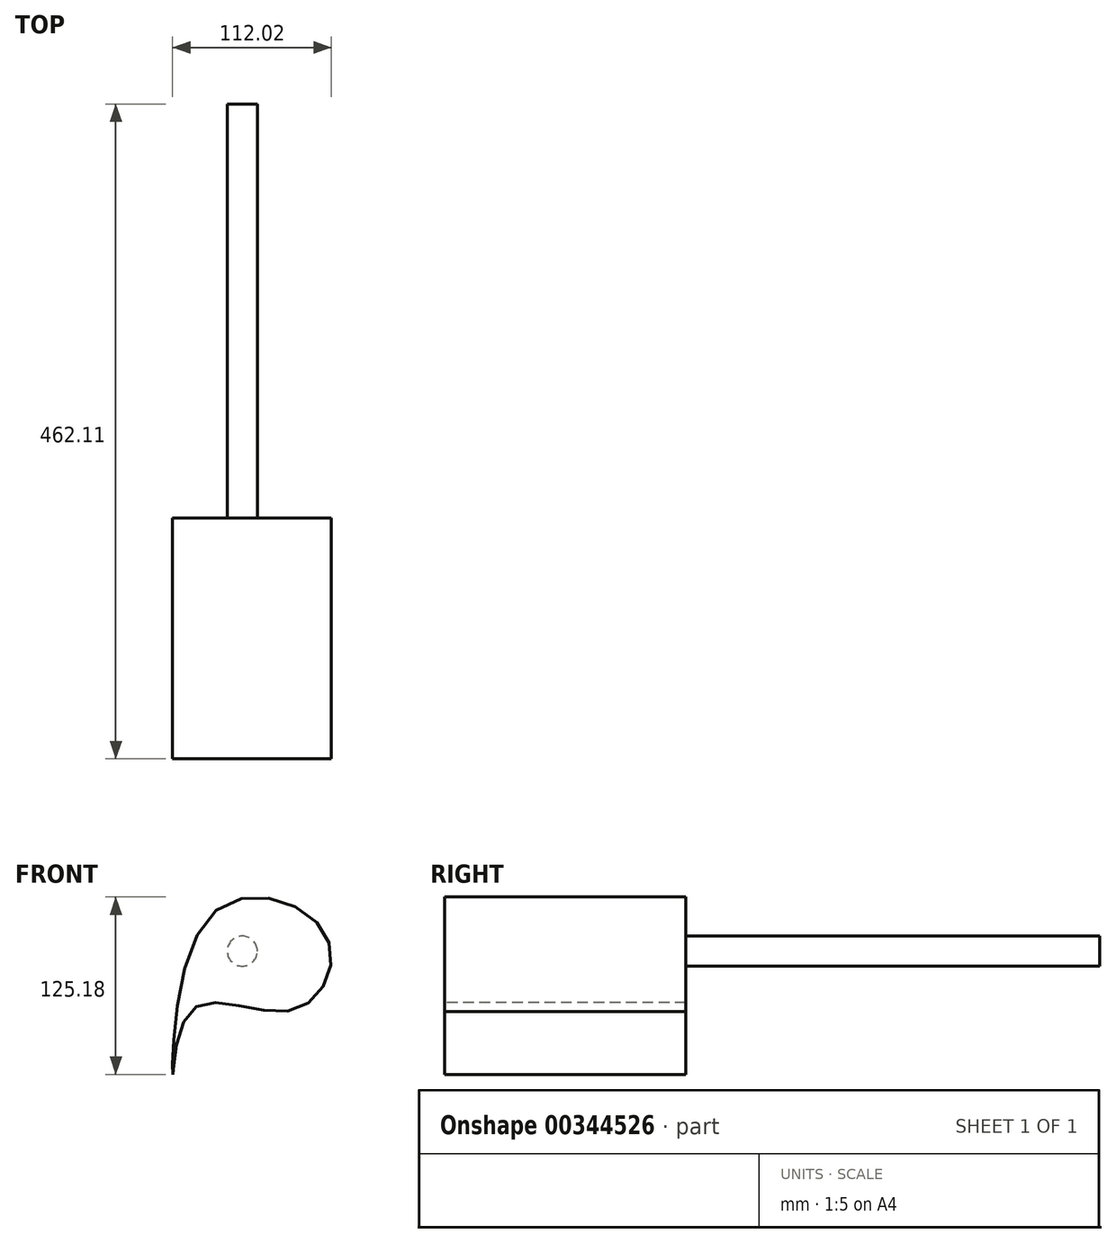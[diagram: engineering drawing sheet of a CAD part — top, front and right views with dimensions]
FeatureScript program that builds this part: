
annotation { "Feature Type Name" : "Feature", "Feature Type Description" : "" }
export const myFeature = defineFeature(function(context is Context, id is Id, definition is map)
    precondition{}
    {
        {
            var Q0;
            Q0=qCreatedBy(makeId("Front.planeOp"),FACE);
            var sketch = newSketch(context, id + "F0", { "sketchPlane" : qUnion([Q0])});
            skFitSpline(sketch, "E0", {"points": [v(-49, -45.53) * mm, v(-35.61, 0) * mm, v(36.14, 0) * mm, v(59.24, 52.42) * mm, v(-21.64, 67.33) * mm, v(-49, -45.53) * mm]});
            skSolve(sketch);
        }
        {
            var Q0;
            Q0 = qSketchRegion(id + "F0", true);
            extrude(context, id + "F1", {"entities" : qUnion([Q0]), "oppositeDirection" : true, "depth" : 170.05 * mm});
        }
        {
            var Q0;
            Q0=makeQuery(id+"F1.opExtrude","CAP_FACE",FACE,{"disambiguationData":[OSD([sQuery(id+"F0.wireOp",EDGE,"E0")])],"isStart":false});
            var sketch = newSketch(context, id + "F2", { "sketchPlane" : qUnion([Q0])});
            skCircle(sketch, "E1", {"center": v(0, 41.46) * mm, "radius": 10.63 * mm});
            skSolve(sketch);
        }
        {
            var Q0;
            Q0=makeQuery(id+"F2.imprint","IMPRINT",FACE,{"disambiguationData":[TD([[makeQuery(id+"F2.imprint","IMPRINT",EDGE,{"derivedFrom":sQuery(id+"F2.wireOp",EDGE,"E1")}),1.0]])]});
            var Q1;
            Q1=sQuery(id+"F2.wireOp",EDGE,"E1");
            extrude(context, id + "F3", {"entities" : qUnion([Q0]), "operationType" : NewBodyOperationType.ADD, "surfaceEntities" : qUnion([Q1]), "depth" : 292.05 * mm});
        }
    });
